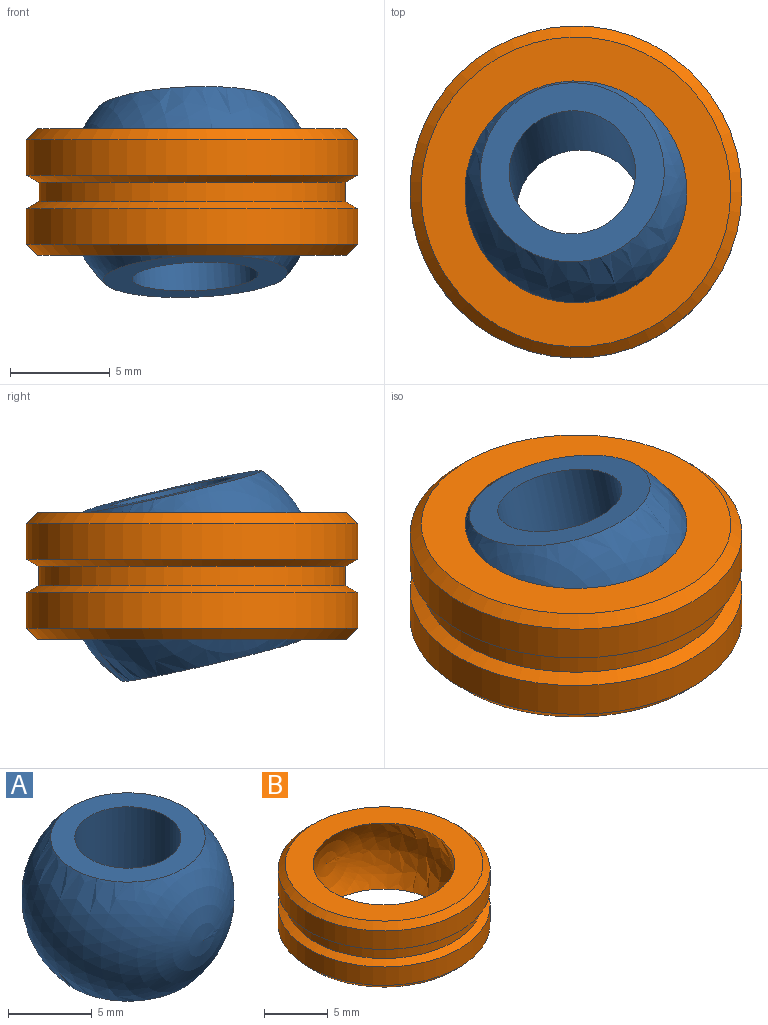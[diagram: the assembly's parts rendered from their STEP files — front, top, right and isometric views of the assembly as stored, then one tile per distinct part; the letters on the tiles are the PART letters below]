
ASSEMBLY  parts=2 mates=1
PART A: 4 faces, bbox 12.7x12.7x12.7 mm
  f0: sphere r=6.35mm, area 347.6mm2, adj f2,f3
  f1: cylinder r=3.17mm len=8.71mm, axis (0,0,1), area 173.8mm2, adj f2,f3
  f2: plane 9.24x9.24mm, normal (0,0,1), area 35.4mm2, adj f0,f1
  f3: plane 9.24x9.24mm, normal (0,0,-1), area 35.4mm2, adj f0,f1
PART B: 10 faces, bbox 16.7x16.7x12.8 mm
  f0: cylinder r=8.33mm len=16.67mm, axis (0,0,-1), area 92.5mm2, adj f5,f7
  f1: cylinder r=8.33mm len=16.67mm, axis (0,0,-1), area 92.5mm2, adj f6,f9
  f2: plane 15.55x15.55mm, normal (0,0,1), area 92.4mm2, adj f4,f5
  f3: plane 15.55x15.55mm, normal (0,0,-1), area 92.4mm2, adj f4,f6
  f4: sphere r=6.41mm, area 255.9mm2, adj f2,f3
  f5: cone r=7.77mm half-angle=45deg, axis (0,0,-1), area 40mm2, adj f0,f2
  f6: cone r=8.33mm half-angle=45deg, axis (0,0,1), area 40mm2, adj f1,f3
  f7: cone r=8.33mm half-angle=60deg, axis (0,0,1), area 37.2mm2, adj f0,f8
  f8: cylinder r=7.69mm len=15.39mm, axis (0,0,1), area 46.4mm2, adj f7,f9
  f9: cone r=7.69mm half-angle=60deg, axis (0,0,-1), area 37.2mm2, adj f1,f8
PLACE A rot(axis=(-0.14,-0.14,-0.98),69.8deg) t=(-5.26,12.91,0.99)mm
PLACE B t=(-5.26,12.91,0.99)mm
MATE ball A.f1 <-> B.f0  axis (-0.04,0.22,0.97) through (-5.26,12.91,0.99)mm
